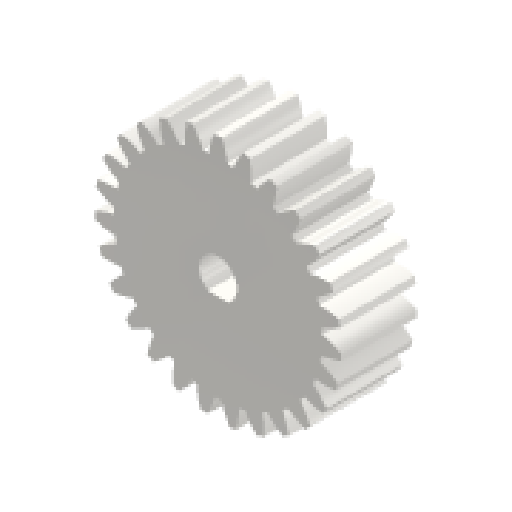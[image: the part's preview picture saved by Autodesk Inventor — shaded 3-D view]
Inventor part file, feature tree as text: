
AUTODESK INVENTOR PART (.ipt)
format: ipt  version: 2024.1 (Build 281209000, 209)  size: 324,096 bytes
history: native  units: mm (DEFAULTED — no unit token found)
features: plane x3, other x3, extrude x2, sketch x2, chamfer x1, projected_geometry x1
ambient origin geometry x8: Origin, YZ Plane, XZ Plane, XY Plane, X Axis, Y Axis, Z Axis, Center Point
bodies: Solid1 (feature_tree)
feature tree (12):
  extrude  "Extrusion1"  Depth=10.0mm TaperAngle=0.0deg
  plane  "Work Plane2"
  plane  "Work Plane8"
  plane  "Work Plane9"
  other  "Stirnzahnrad"
  extrude  "Extrusion2"  Depth=10.0mm TaperAngle=0.0deg
  chamfer  "Fasen1"  Distance=35.0mm
  sketch  "Sketch1"  dims[d0=32.62166mm d1=10.0mm d2=0.0mm]
  other  "Srf1"
  sketch  "Skizze3"  dims[d3=30.375mm d4=10.0mm d5=0.0mm d16=35.0mm d17=0.0mm d34=1.163553mm d39=0.0mm d41=0.0mm d43=35.0mm d46=35.0mm d47=0.0mm d48=0.0mm d49=5.0mm d50=8.0mm d51=0.0mm d52=2.1mm d53=1.0mm d54=2.0mm d55=45.0deg]
  projected_geometry  "Projizierte Kontur1"
  other  "Flankendurchmesser"
